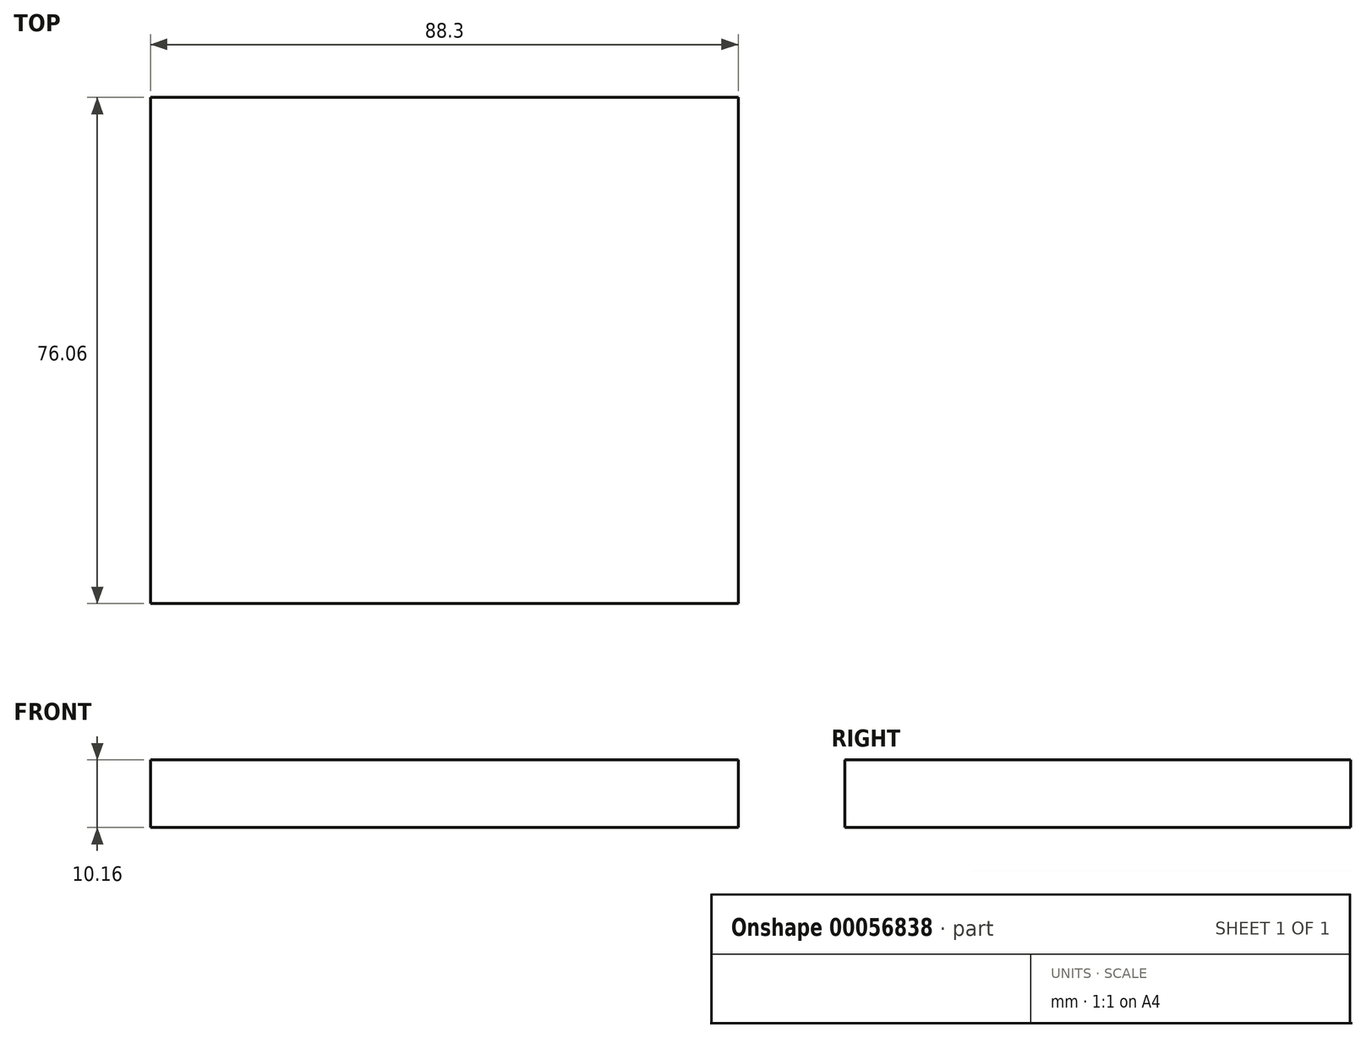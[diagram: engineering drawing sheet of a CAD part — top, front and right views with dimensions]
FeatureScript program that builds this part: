
annotation { "Feature Type Name" : "Feature", "Feature Type Description" : "" }
export const myFeature = defineFeature(function(context is Context, id is Id, definition is map)
    precondition{}
    {
        {
            var Q0;
            Q0=qCreatedBy(makeId("Top.planeOp"),FACE);
            var sketch = newSketch(context, id + "F0", { "sketchPlane" : qUnion([Q0])});
            skLineSegment(sketch, "E0.bottom", {"start": v(0, 0) * mm, "end": v(-88.3, 0) * mm});
            skLineSegment(sketch, "E0.top", {"start": v(0, 76.06) * mm, "end": v(-88.3, 76.06) * mm});
            skLineSegment(sketch, "E0.left", {"start": v(0, 0) * mm, "end": v(0, 76.06) * mm});
            skLineSegment(sketch, "E0.right", {"start": v(-88.3, 0) * mm, "end": v(-88.3, 76.06) * mm});
            skSolve(sketch);
        }
        {
            var Q0;
            Q0 = qSketchRegion(id + "F0", true);
            extrude(context, id + "F1", {"entities" : qUnion([Q0]), "depth" : 10.16 * mm});
        }
    });
